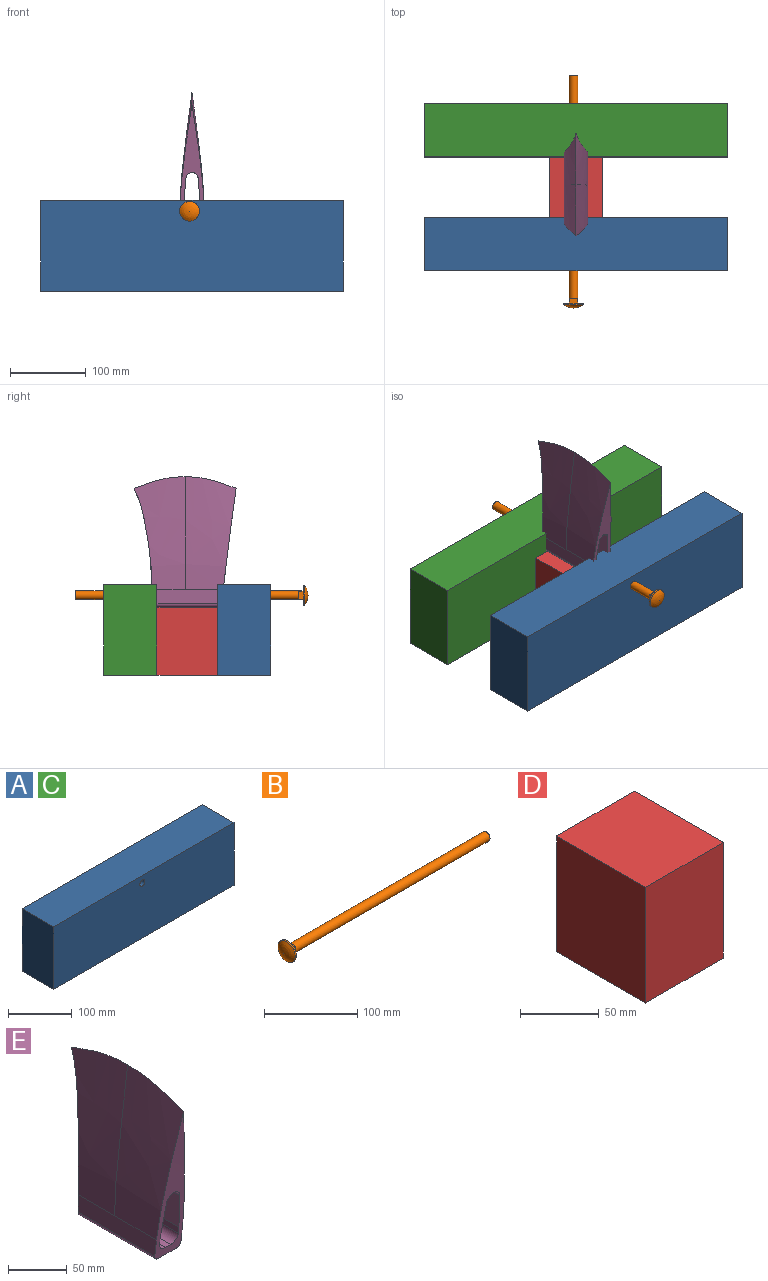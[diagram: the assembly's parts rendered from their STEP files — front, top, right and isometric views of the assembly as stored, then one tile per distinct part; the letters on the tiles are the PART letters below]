
ASSEMBLY  parts=5 mates=3
PART A: 7 faces, bbox 400x70x120 mm
  f0: plane 400x120mm, normal (0,1,0), area 47896.1mm2, adj f1,f3,f4,f5,f6
  f1: plane 120x70mm, normal (-1,0,0), area 8400mm2, adj f0,f2,f4,f5
  f2: plane 400x120mm, normal (0,-1,0), area 47896.1mm2, adj f1,f3,f4,f5,f6
  f3: plane 120x70mm, normal (1,0,0), area 8400mm2, adj f0,f2,f4,f5
  f4: plane 400x70mm, normal (0,0,1), area 28000mm2, adj f0,f1,f2,f3
  f5: plane 400x70mm, normal (0,0,-1), area 28000mm2, adj f0,f1,f2,f3
  f6: cylinder r=5.75mm len=70mm, axis (0,1,0), area 2529mm2, adj f0,f2
PART B: 14 faces, bbox 306.5x26x26 mm
  f0: plane 11.74x11.74mm, normal (1,0,0), area 33.5mm2, adj f1,f2,f3,f4,f6,f10,f11,f12
  f1: cylinder r=8mm len=6mm, axis (-1,0,0), area 3.7mm2, adj f0,f7,f12,f13
  f2: cylinder r=8mm len=6mm, axis (-1,0,0), area 3.7mm2, adj f0,f7,f11,f12
  f3: cylinder r=8mm len=6mm, axis (-1,0,0), area 3.7mm2, adj f0,f7,f10,f11
  f4: cylinder r=8mm len=6mm, axis (-1,0,0), area 3.7mm2, adj f0,f7,f10,f13
  f5: plane 11.5x11.5mm, normal (1,0,0), area 103.9mm2, adj f6
  f6: cylinder r=5.75mm len=294mm, axis (-1,0,0), area 10621.7mm2, adj f0,f5
  f7: plane 26x26mm, normal (1,0,0), area 393.5mm2, adj f1,f2,f3,f4,f8,f10,f11,f12
  f8: cylinder r=13mm len=26mm, axis (-1,0,0), area 163.4mm2, adj f7,f9
  f9: revolved ~26x26mm, area 593.9mm2, adj f8
  f10: plane 10.87x6mm, normal (0,-1,0), area 65.2mm2, adj f0,f3,f4,f7
  f11: plane 10.87x6mm, normal (0,0,-1), area 65.2mm2, adj f0,f2,f3,f7
  f12: plane 10.87x6mm, normal (0,1,0), area 65.2mm2, adj f0,f1,f2,f7
  f13: plane 10.87x6mm, normal (0,0,1), area 65.2mm2, adj f0,f1,f4,f7
PART C: same geometry as A
PART D: 6 faces, bbox 70x80x90 mm
  f0: plane 90x70mm, normal (0,1,0), area 6300mm2, adj f1,f3,f4,f5
  f1: plane 90x80mm, normal (-1,0,0), area 7200mm2, adj f0,f2,f4,f5
  f2: plane 90x70mm, normal (0,-1,0), area 6300mm2, adj f1,f3,f4,f5
  f3: plane 90x80mm, normal (1,0,0), area 7200mm2, adj f0,f2,f4,f5
  f4: plane 80x70mm, normal (0,0,1), area 5600mm2, adj f0,f1,f2,f3
  f5: plane 80x70mm, normal (0,0,-1), area 5600mm2, adj f0,f1,f2,f3
PART E: 22 faces, bbox 31.5x134.9x172.5 mm
  f0: plane 100.04x36.7mm, normal (1,0,-0.09), area 3568.7mm2, adj f1,f9,f10,f11
  f1: cylinder r=8mm len=101.6mm, axis (0,-1,0), area 1196.6mm2, adj f0,f2,f10,f11
  f2: plane 101.6x0.14mm, normal (0,0,-1), area 14.2mm2, adj f1,f3,f10,f11
  f3: cylinder r=8mm len=101.6mm, axis (0,-1,0), area 1196.6mm2, adj f2,f4,f10,f11
  f4: plane 100.04x36.7mm, normal (-1,0,-0.09), area 3568.7mm2, adj f3,f5,f10,f11
  f5: plane 94.2x7mm, normal (-1,0,0), area 656.3mm2, adj f4,f6,f10,f11
  f6: cylinder r=8mm len=93.34mm, axis (0,-1,0), area 1167mm2, adj f5,f7,f10,f11
  f7: plane 92.4x6.5mm, normal (0,0,1), area 600.6mm2, adj f6,f8,f10,f11
  f8: cylinder r=8mm len=93.34mm, axis (0,-1,0), area 1167mm2, adj f7,f9,f10,f11
  f9: plane 94.2x7mm, normal (1,0,0), area 656.3mm2, adj f0,f8,f10,f11
  f10: extruded ~156.56x31.5mm, area 2193.6mm2, adj f0,f1,f2,f3,f4,f5,f6,f7
  f11: extruded ~157.31x31.5mm, area 2122.4mm2, adj f0,f1,f2,f3,f4,f5,f6,f7
  f12: bspline ~149.5x67.44mm, area 8640.8mm2, adj f11,f13,f18,f20
  f13: bspline ~149.5x67.44mm, area 8639.1mm2, adj f11,f12,f14,f21
  f14: plane 94.21x18.02mm, normal (1,0,0), area 1676mm2, adj f10,f11,f13,f15,f21
  f15: cylinder r=5mm len=92.06mm, axis (0,-1,0), area 720.8mm2, adj f10,f11,f14,f16
  f16: plane 91.5x21.5mm, normal (0,0,-1), area 1967.2mm2, adj f10,f11,f15,f17
  f17: cylinder r=5mm len=92.06mm, axis (0,-1,0), area 720.8mm2, adj f10,f11,f16,f18
  f18: plane 94.21x18.02mm, normal (-1,0,0), area 1676mm2, adj f10,f11,f12,f17,f20
  f19: plane 0.74x0.21mm, normal (0,1,0), area 0.1mm2, adj f10,f20,f21
  f20: bspline ~149.5x67.44mm, area 7576.8mm2, adj f10,f12,f18,f19,f21
  f21: bspline ~149.5x67.44mm, area 7576.8mm2, adj f10,f13,f14,f19,f20
PLACE A t=(0,-75,15)mm
PLACE B rot(axis=(0.58,0.58,0.58),120deg) t=(-3.25,-6.25,60.71)mm
PLACE C t=(0,75,15)mm
PLACE D at identity fixed
PLACE E t=(0,2.89,130.96)mm
MATE fastened D.f2 <-> A.f0  axis (0,-1,0) through (0,-40,-45)mm
MATE fastened C.f2 <-> D.f0  axis (0,-1,0) through (0,40,-45)mm
MATE fastened E.f8 <-> B.f1  axis (0,-1,0) through (-3.25,0,60.71)mm
